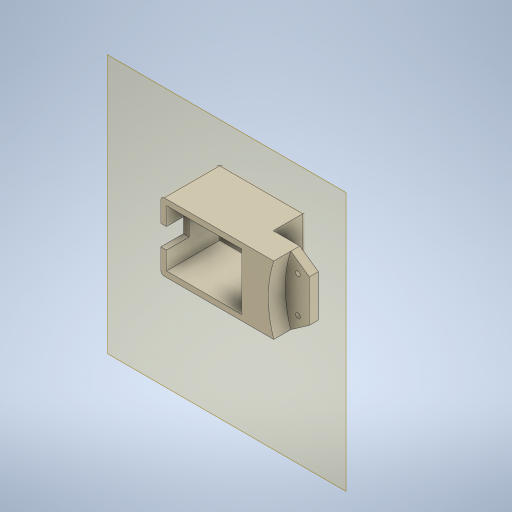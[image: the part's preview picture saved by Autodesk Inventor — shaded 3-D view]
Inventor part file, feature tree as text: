
AUTODESK INVENTOR PART (.ipt)
format: ipt  version: 2024 (Build 280153000, 153)  size: 795,648 bytes
history: native  units: mm
features: reference x8, extrude x7, sketch x7, projected_geometry x4, other x4, plane x2, fillet x1
ambient origin geometry x8: Origin, YZ Plane, XZ Plane, XY Plane, X Axis, Y Axis, Z Axis, Center Point
bodies: Solid1 (feature_tree)
feature tree (33):
  plane  "Work Plane1"
  plane  "Work Plane2"
  extrude  "Extrusion1"  Depth=30.0mm
  extrude  "Extrusion2"  Depth=60.0mm
  extrude  "Extrusion3"  Depth=4.2mm
  extrude  "Extrusion4"  Depth=20.0mm
  extrude  "Extrusion5"  Depth=20.0mm
  extrude  "Extrusion6"  Depth=10.0mm
  fillet  "Fillet1"  Radius=14.0mm
  extrude  "Extrusion7"  Depth=8.0mm TaperAngle=0.0deg
  sketch  "Sketch1"  dims[d0=30.0mm d1=30.0mm]
  reference  "Reference1"
  sketch  "Sketch2"  dims[d2=95.0mm d3=60.0mm]
  reference  "Reference2"
  projected_geometry  "Projected Loop1"
  sketch  "Sketch3"  dims[d4=51.0mm d5=0.0mm d6=4.2mm]
  sketch  "Sketch4"  dims[d7=14.0mm d8=20.0mm]
  reference  "Reference3"
  sketch  "Sketch5"  dims[d9=25.307274mm d10=20.0mm]
  projected_geometry  "Projected Loop6"
  projected_geometry  "Projected Loop7"
  sketch  "Sketch6"  dims[d11=25.307274mm d12=10.0mm d13=14.0mm]
  projected_geometry  "Projected Loop8"
  reference  "Reference4"
  reference  "Reference5"
  reference  "Reference6"
  reference  "Reference7"
  reference  "Reference8"
  sketch  "Sketch7"  dims[d14=10.0mm d15=8.0mm d16=0.0mm d17=43.0mm d18=43.0mm d21=24.0mm d22=0.0mm d24=5.0mm d25=0.0mm d26=30.0mm d27=0.0mm d28=0.0mm d29=40.0mm d30=15.0mm d31=5.0mm d32=0.2mm d33=0.2mm d34=0.2mm d35=0.2mm d36=5.0mm d37=0.0mm d39=0.5mm d40=3.0mm d41=20.0mm d42=18.0mm d43=0.0mm d44=0.0mm]
  other  "<userpath>\Documents\Inventor\robot arm\base-new\base_assembly.iam"
  other  "base_assembly.iam"
  other  "base-bottom-plate:1"
  other  "stepper motor:1"
